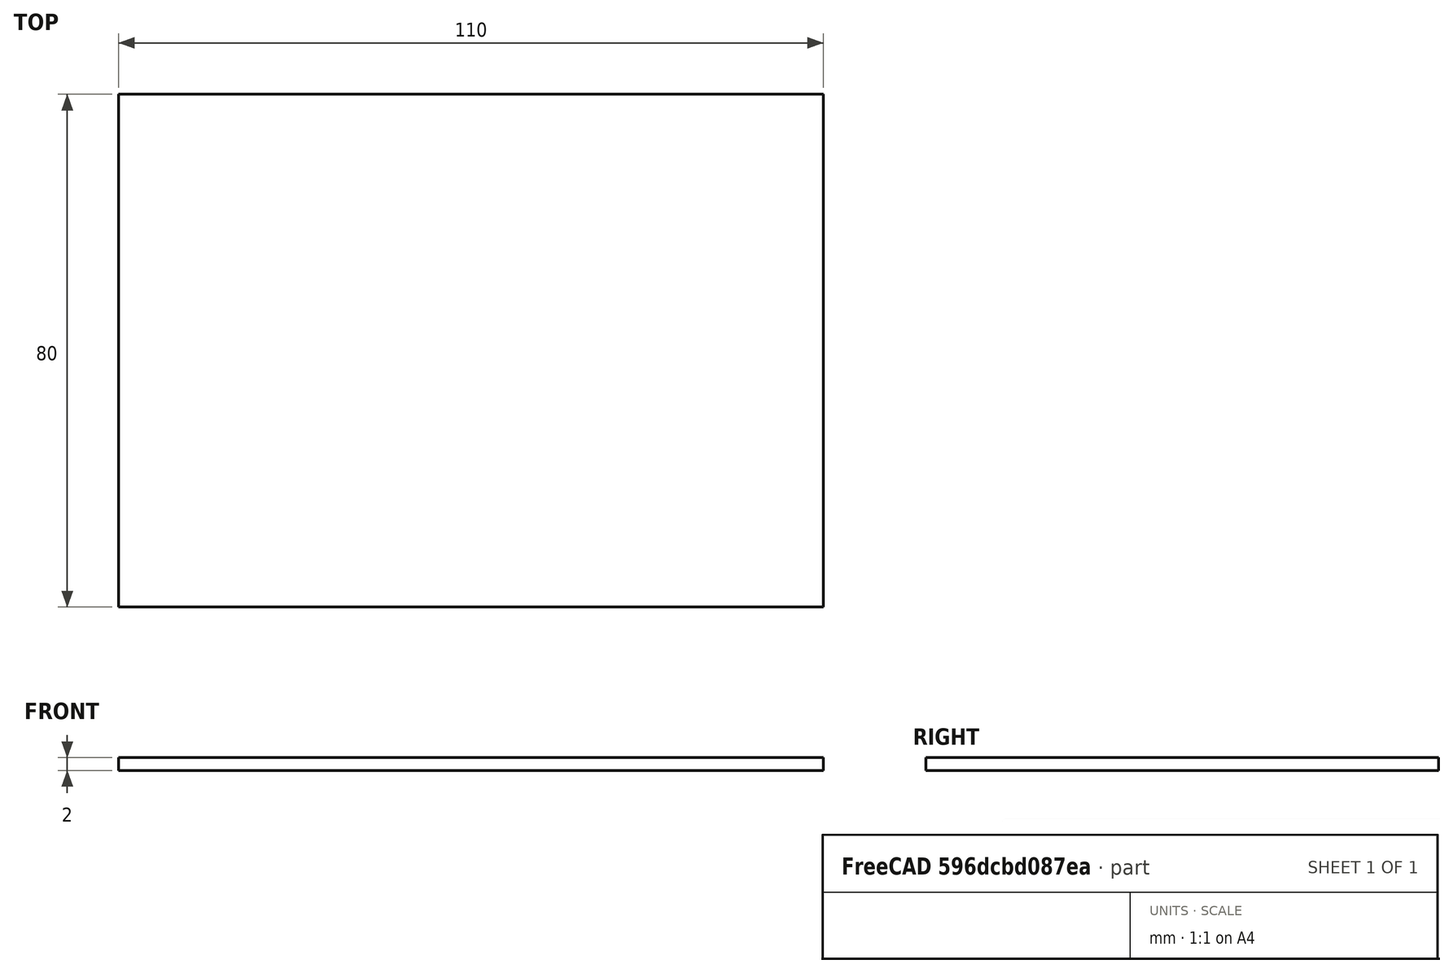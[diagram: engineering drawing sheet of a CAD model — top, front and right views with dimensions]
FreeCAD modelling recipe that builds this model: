
FCSTD DOCUMENT  (FreeCAD 0.18R16146 (Git))
Label: v_w-tapa-paso 2
License: All rights reserved
LicenseURL: http://en.wikipedia.org/wiki/All_rights_reserved
objects: Sketcher::SketchObject×2, PartDesign::Pad×1, PartDesign::Body×1
note: 5 computed .brp shape members not serialized (recipe doc carries the construction recipe); baked Part::Feature solids carry a one-line shape summary decoded from their .brp

FEATURE [Sketcher::SketchObject] Sketch
  MapMode = 5
  Support = -> [XY_Plane]
  sketch-geometry (4):
    g0: LineSegment StartX=-55 StartY=-40 StartZ=0 EndX=55 EndY=-40 EndZ=0
    g1: LineSegment StartX=55 StartY=-40 StartZ=0 EndX=55 EndY=40 EndZ=0
    g2: LineSegment StartX=55 StartY=40 StartZ=0 EndX=-55 EndY=40 EndZ=0
    g3: LineSegment StartX=-55 StartY=40 StartZ=0 EndX=-55 EndY=-40 EndZ=0
  constraints (12):
    c: Coincident(g0,g1)
    c: Coincident(g1,g2)
    c: Coincident(g2,g3)
    c: Coincident(g3,g0)
    c: Horizontal(g0)
    c: Horizontal(g2)
    c: Vertical(g1)
    c: Vertical(g3)
    c: DistanceX(g-1,g1) = 55
    c: DistanceY(g-1,g1) = 40
    c: DistanceX(g2,g2) = 110
    c: DistanceY(g1,g1) = 80
FEATURE [PartDesign::Pad] Pad
  Length = 2
  Length2 = 100
  Profile = -> Sketch
  Type = 0
FEATURE [Sketcher::SketchObject] Sketch001
  MapMode = 5
  Placement = pos=(0,0,2) rot=(0,0,1;0rad)
  Support = -> [Pad]
  sketch-geometry (4):
    g0: Circle CenterX=46 CenterY=31 CenterZ=0 NormalX=0 NormalY=0 NormalZ=1 AngleXU=0 Radius=2.1
    g1: Circle CenterX=-46 CenterY=31 CenterZ=0 NormalX=0 NormalY=0 NormalZ=1 AngleXU=0 Radius=2.1
    g2: Circle CenterX=-46 CenterY=-31 CenterZ=0 NormalX=0 NormalY=0 NormalZ=1 AngleXU=0 Radius=2.1
    g3: Circle CenterX=46 CenterY=-31 CenterZ=0 NormalX=0 NormalY=0 NormalZ=1 AngleXU=0 Radius=2.1
  constraints (9):
    c: Radius(g0) = 2.1
    c: DistanceX(g-1,g0) = 46
    c: DistanceY(g-1,g0) = 31
    c: Equal(g0,g1) = 2.1
    c: Equal(g0,g2) = 2.1
    c: Equal(g0,g3) = 2.1
    c: Symmetric(g0,g1,g-2)
    c: Symmetric(g1,g2,g-1)
    c: Symmetric(g2,g3,g-2)
FEATURE [PartDesign::Body] Body
  Group = -> [Sketch,Pad,Sketch001]
  Origin = -> Origin
  Tip = -> Pad
